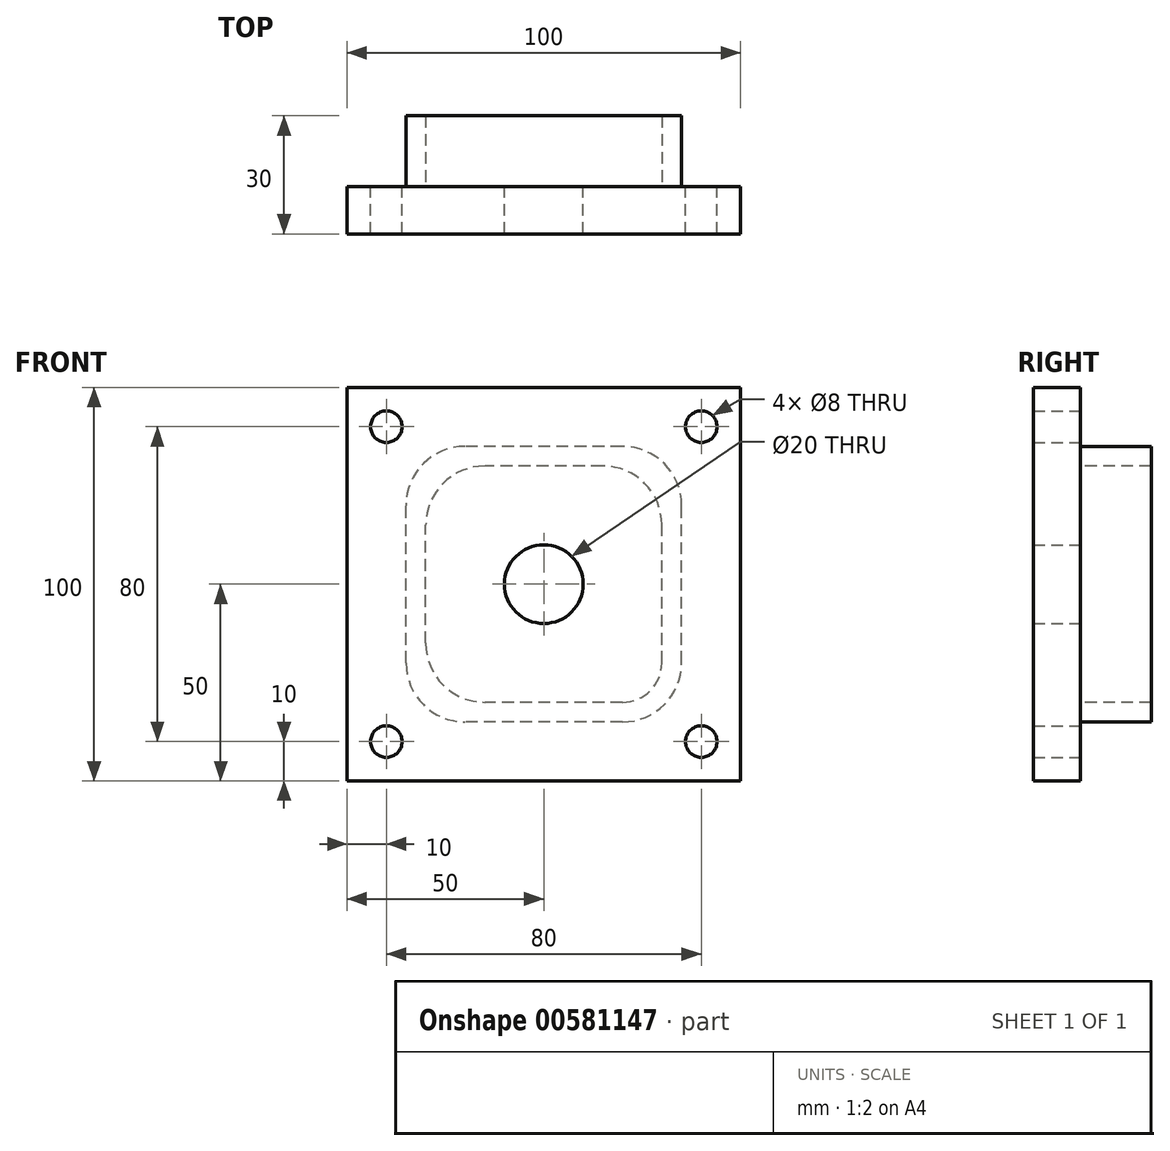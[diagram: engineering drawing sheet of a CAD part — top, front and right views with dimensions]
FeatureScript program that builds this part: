
annotation { "Feature Type Name" : "Feature", "Feature Type Description" : "" }
export const myFeature = defineFeature(function(context is Context, id is Id, definition is map)
    precondition{}
    {
        {
            var Q0;
            Q0=qCreatedBy(makeId("Front.planeOp"),FACE);
            var sketch = newSketch(context, id + "F0", { "sketchPlane" : qUnion([Q0])});
            skLineSegment(sketch, "E0.bottom", {"start": v(50, -50) * mm, "end": v(-50, -50) * mm});
            skLineSegment(sketch, "E0.top", {"start": v(50, 50) * mm, "end": v(-50, 50) * mm});
            skLineSegment(sketch, "E0.left", {"start": v(50, -50) * mm, "end": v(50, 50) * mm});
            skLineSegment(sketch, "E0.right", {"start": v(-50, -50) * mm, "end": v(-50, 50) * mm});
            skLineSegment(sketch, "E1", {"start": v(0, -50) * mm, "end": v(0, 0) * mm, "construction": true});
            skLineSegment(sketch, "E2", {"start": v(0, 0) * mm, "end": v(50, 0) * mm, "construction": true});
            skSolve(sketch);
        }
        {
            var Q0;
            Q0=makeQuery(id+"F0.imprint","IMPRINT",FACE,{"disambiguationData":[TD([[makeQuery(id+"F0.imprint","IMPRINT",EDGE,{"derivedFrom":sQuery(id+"F0.wireOp",EDGE,"E0.bottom")}),-1.0]])]});
            extrude(context, id + "F1", {"entities" : qUnion([Q0]), "depth" : 12 * mm, "offsetDistance" : 25 * mm});
        }
        {
            var Q0;
            Q0=makeQuery(id+"F1.opExtrude","CAP_FACE",FACE,{"disambiguationData":[OSD([sQuery(id+"F0.wireOp",EDGE,"E0.bottom"),sQuery(id+"F0.wireOp",EDGE,"E0.top"),sQuery(id+"F0.wireOp",EDGE,"E0.left"),sQuery(id+"F0.wireOp",EDGE,"E0.right")])],"isStart":true});
            var sketch = newSketch(context, id + "F2", { "sketchPlane" : qUnion([Q0])});
            skCircle(sketch, "E3", {"center": v(-40, 40) * mm, "radius": 4 * mm});
            skCircle(sketch, "E4", {"center": v(-40, -40) * mm, "radius": 4 * mm});
            skCircle(sketch, "E5", {"center": v(40, 40) * mm, "radius": 4 * mm});
            skCircle(sketch, "E6", {"center": v(40, -40) * mm, "radius": 4 * mm});
            skCircle(sketch, "E7", {"center": v(0, 0) * mm, "radius": 10 * mm});
            skSolve(sketch);
        }
        {
            var Q0;
            Q0=makeQuery(id+"F2.imprint","IMPRINT",FACE,{"disambiguationData":[TD([[makeQuery(id+"F2.imprint","IMPRINT",EDGE,{"derivedFrom":sQuery(id+"F2.wireOp",EDGE,"E4")}),1.0]])]});
            var Q1;
            Q1=makeQuery(id+"F2.imprint","IMPRINT",FACE,{"disambiguationData":[TD([[makeQuery(id+"F2.imprint","IMPRINT",EDGE,{"derivedFrom":sQuery(id+"F2.wireOp",EDGE,"E3")}),1.0]])]});
            var Q2;
            Q2=makeQuery(id+"F2.imprint","IMPRINT",FACE,{"disambiguationData":[TD([[makeQuery(id+"F2.imprint","IMPRINT",EDGE,{"derivedFrom":sQuery(id+"F2.wireOp",EDGE,"E6")}),1.0]])]});
            var Q3;
            Q3=makeQuery(id+"F2.imprint","IMPRINT",FACE,{"disambiguationData":[TD([[makeQuery(id+"F2.imprint","IMPRINT",EDGE,{"derivedFrom":sQuery(id+"F2.wireOp",EDGE,"E5")}),1.0]])]});
            var Q4;
            Q4=makeQuery(id+"F2.imprint","IMPRINT",FACE,{"disambiguationData":[TD([[makeQuery(id+"F2.imprint","IMPRINT",EDGE,{"derivedFrom":sQuery(id+"F2.wireOp",EDGE,"E7")}),1.0]])]});
            extrude(context, id + "F3", {"entities" : qUnion([Q0, Q1, Q2, Q3, Q4]), "operationType" : NewBodyOperationType.REMOVE, "oppositeDirection" : true, "depth" : 12 * mm, "offsetDistance" : 25 * mm});
        }
        {
            var Q0;
            Q0=makeQuery(id+"F1.opExtrude","CAP_FACE",FACE,{"disambiguationData":[OSD([sQuery(id+"F0.wireOp",EDGE,"E0.bottom"),sQuery(id+"F0.wireOp",EDGE,"E0.top"),sQuery(id+"F0.wireOp",EDGE,"E0.left"),sQuery(id+"F0.wireOp",EDGE,"E0.right")])],"isStart":true});
            var sketch = newSketch(context, id + "F4", { "sketchPlane" : qUnion([Q0])});
            skLineSegment(sketch, "E8.bottom", {"start": v(-20, -35) * mm, "end": v(20, -35) * mm});
            skLineSegment(sketch, "E8.top", {"start": v(-20, 35) * mm, "end": v(20, 35) * mm});
            skLineSegment(sketch, "E8.left", {"start": v(-35, -20) * mm, "end": v(-35, 20) * mm});
            skLineSegment(sketch, "E8.right", {"start": v(35, -20) * mm, "end": v(35, 20) * mm});
            skLineSegment(sketch, "E9.bottom", {"start": v(-20, -30) * mm, "end": v(15, -30) * mm});
            skLineSegment(sketch, "E9.top", {"start": v(-15, 30) * mm, "end": v(15, 30) * mm});
            skLineSegment(sketch, "E9.left", {"start": v(-30, -20) * mm, "end": v(-30, 15) * mm});
            skLineSegment(sketch, "E9.right", {"start": v(30, -15) * mm, "end": v(30, 15) * mm});
            skPoint(sketch, "E10.visualSharp", {"position": v(-35, -35) * mm});
            skArc(sketch, "E10.filletArc", {"start": v(-35, -20) * mm, "mid": v(-30.6, -30.6) * mm, "end": v(-20, -35) * mm});
            skPoint(sketch, "E11.visualSharp", {"position": v(-30, -30) * mm});
            skArc(sketch, "E11.filletArc", {"start": v(-30, -20) * mm, "mid": v(-27.07, -27.07) * mm, "end": v(-20, -30) * mm});
            skPoint(sketch, "E12.visualSharp", {"position": v(-35, 35) * mm});
            skArc(sketch, "E12.filletArc", {"start": v(-20, 35) * mm, "mid": v(-30.6, 30.6) * mm, "end": v(-35, 20) * mm});
            skPoint(sketch, "E13.visualSharp", {"position": v(35, 35) * mm});
            skArc(sketch, "E13.filletArc", {"start": v(35, 20) * mm, "mid": v(30.6, 30.6) * mm, "end": v(20, 35) * mm});
            skPoint(sketch, "E14.visualSharp", {"position": v(35, -35) * mm});
            skArc(sketch, "E14.filletArc", {"start": v(20, -35) * mm, "mid": v(30.6, -30.6) * mm, "end": v(35, -20) * mm});
            skPoint(sketch, "E15.visualSharp", {"position": v(30, -30) * mm});
            skArc(sketch, "E15.filletArc", {"start": v(15, -30) * mm, "mid": v(25.6, -25.6) * mm, "end": v(30, -15) * mm});
            skPoint(sketch, "E16.visualSharp", {"position": v(30, 30) * mm});
            skArc(sketch, "E16.filletArc", {"start": v(30, 15) * mm, "mid": v(25.6, 25.6) * mm, "end": v(15, 30) * mm});
            skPoint(sketch, "E17.visualSharp", {"position": v(-30, 30) * mm});
            skArc(sketch, "E17.filletArc", {"start": v(-15, 30) * mm, "mid": v(-25.6, 25.6) * mm, "end": v(-30, 15) * mm});
            skLineSegment(sketch, "E18", {"start": v(0, -35) * mm, "end": v(0, 0) * mm, "construction": true});
            skLineSegment(sketch, "E19", {"start": v(0, 0) * mm, "end": v(-35, 0) * mm, "construction": true});
            skLineSegment(sketch, "E20", {"start": v(0, 0) * mm, "end": v(-30, 0) * mm, "construction": true});
            skSolve(sketch);
        }
        {
            var Q0;
            Q0=makeQuery(id+"F4.imprint","IMPRINT",FACE,{"disambiguationData":[TD([[makeQuery(id+"F4.imprint","IMPRINT",EDGE,{"derivedFrom":sQuery(id+"F4.wireOp",EDGE,"E8.bottom")}),1.0]])]});
            extrude(context, id + "F5", {"entities" : qUnion([Q0]), "operationType" : NewBodyOperationType.ADD, "depth" : 18 * mm, "offsetDistance" : 25 * mm});
        }
    });
